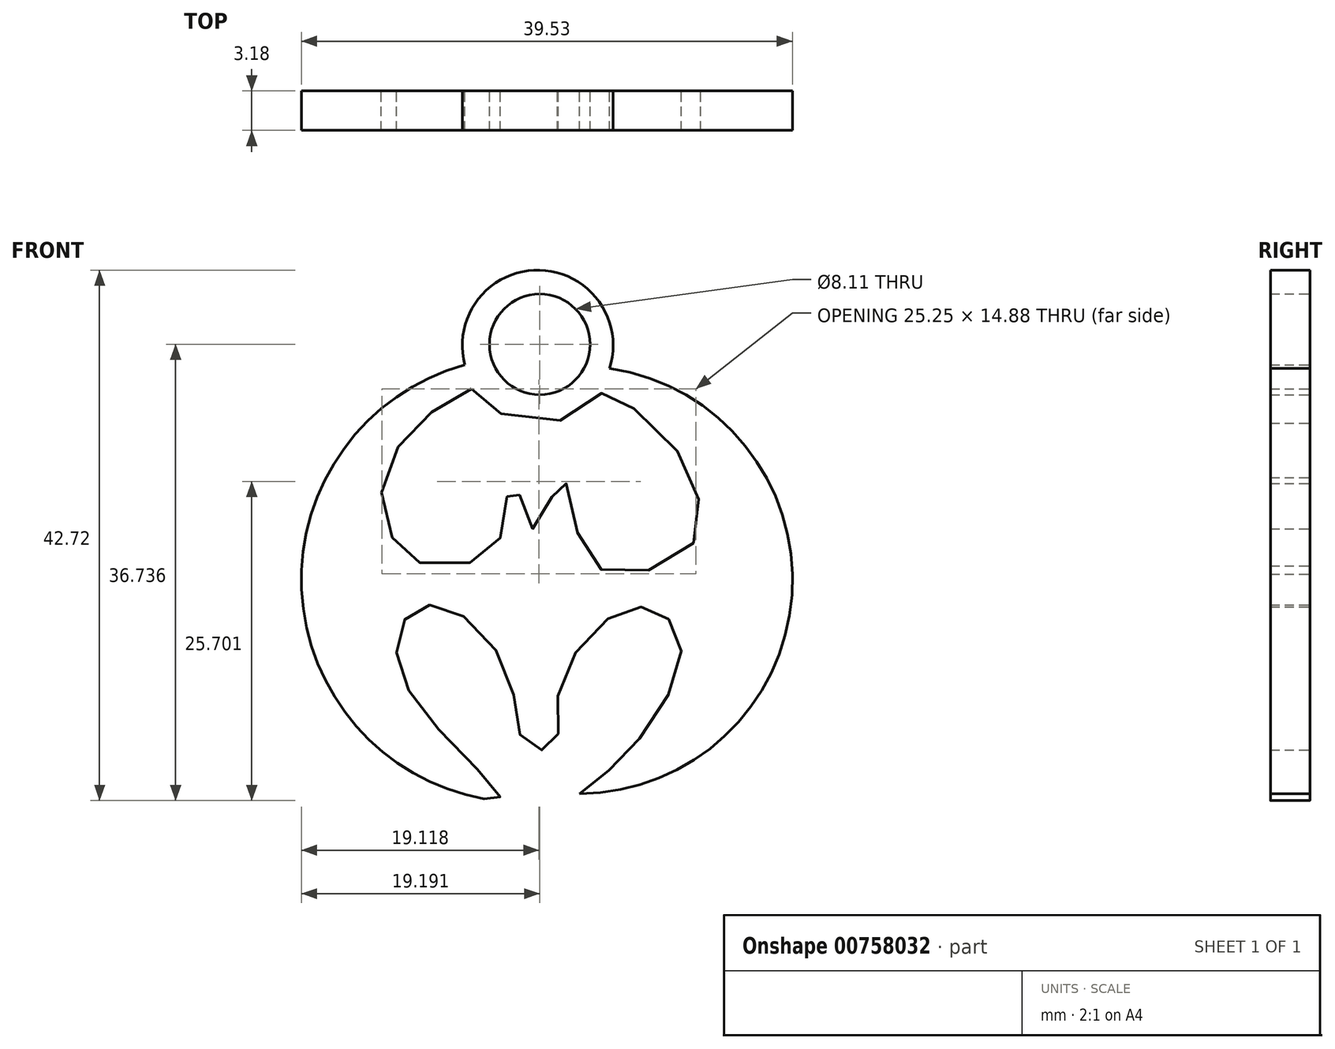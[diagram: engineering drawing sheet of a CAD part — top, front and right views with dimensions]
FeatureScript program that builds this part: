
annotation { "Feature Type Name" : "Feature", "Feature Type Description" : "" }
export const myFeature = defineFeature(function(context is Context, id is Id, definition is map)
    precondition{}
    {
        {
            var Q0;
            Q0=qCreatedBy(makeId("Front.planeOp"),FACE);
            var sketch = newSketch(context, id + "F0", { "sketchPlane" : qUnion([Q0])});
            skArc(sketch, "E0", {"start": v(-6.52, 18.3) * mm, "mid": v(-19.67, 0.2) * mm, "end": v(-4.96, -16.66) * mm});
            skArc(sketch, "E1", {"start": v(2.71, -16.24) * mm, "mid": v(19.81, -0.23) * mm, "end": v(5.13, 18.01) * mm});
            skFitSpline(sketch, "E2", {"points": [v(-6, 16.35) * mm, v(-8.65, 14.9) * mm, v(-11.24, 12.55) * mm, v(-12.98, 9.44) * mm, v(-13.06, 6.1) * mm, v(-11.77, 3.5) * mm, v(-10.17, 2.37) * mm, v(-6.45, 2.3) * mm, v(-4.17, 3.5) * mm, v(-3.33, 5.71) * mm, v(-3.03, 8.14) * mm, v(-2.65, 8.75) * mm, v(-1.89, 6.93) * mm, v(-1.28, 5.18) * mm, v(0, 5.64) * mm, v(0.62, 8.68) * mm, v(1.07, 9.2) * mm, v(2.29, 7.3) * mm, v(2.82, 3.36) * mm, v(5.03, 1.6) * mm, v(8.52, 1.84) * mm, v(11.94, 4.04) * mm, v(12.4, 6.78) * mm, v(11.18, 10.5) * mm, v(7.6, 14.3) * mm, v(4.8, 16.35) * mm, v(4.04, 15.21) * mm, v(-1.13, 13.62) * mm, v(-4.7, 15.21) * mm, v(-6, 16.35) * mm]});
            skFitSpline(sketch, "E3", {"points": [v(-4.96, -16.66) * mm, v(-3.67, -16.66) * mm, v(-7.78, -12) * mm, v(-11.96, -5.47) * mm, v(-10.92, -1.69) * mm, v(-7.7, -1.37) * mm, v(-2.86, -7.08) * mm, v(-1.58, -12.32) * mm, v(0.68, -12.32) * mm, v(1, -8.13) * mm, v(5.35, -1.93) * mm, v(8.97, -1.52) * mm, v(10.9, -4.82) * mm, v(7.04, -12.4) * mm, v(2.71, -16.24) * mm], "startDerivative": vector(49.12, -9.21) * mm, "endDerivative": vector(-53.86, -40.26) * mm});
            skCircle(sketch, "E4", {"center": v(-0.49, 19.95) * mm, "radius": 4.05 * mm});
            skArc(sketch, "E5", {"start": v(5.13, 18.01) * mm, "mid": v(-0.5, 25.92) * mm, "end": v(-6.52, 18.3) * mm});
            skSolve(sketch);
        }
        {
            var Q0;
            Q0=makeQuery(id+"F0.imprint","IMPRINT",FACE,{"disambiguationData":[TD([[makeQuery(id+"F0.imprint","IMPRINT",EDGE,{"derivedFrom":sQuery(id+"F0.wireOp",EDGE,"E0")}),1.0]])]});
            extrude(context, id + "F1", {"entities" : qUnion([Q0]), "depth" : 3.17 * mm, "offsetDistance" : 25.4 * mm});
        }
    });
